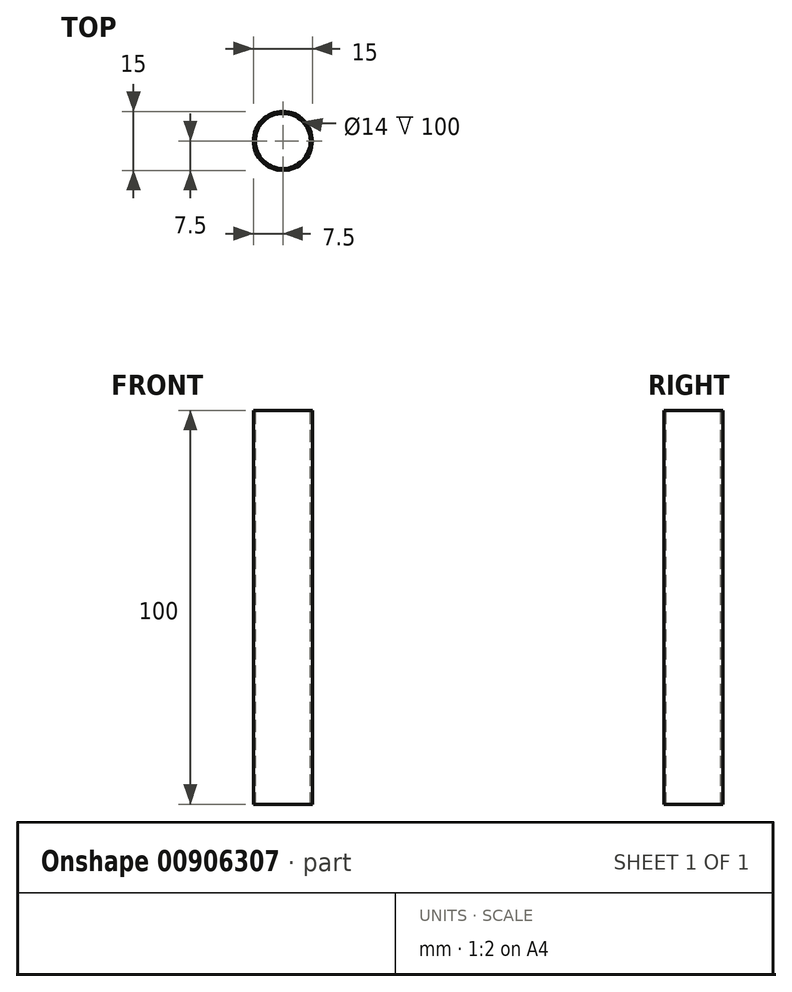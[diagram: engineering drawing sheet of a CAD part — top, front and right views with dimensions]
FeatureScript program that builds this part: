
annotation { "Feature Type Name" : "Feature", "Feature Type Description" : "" }
export const myFeature = defineFeature(function(context is Context, id is Id, definition is map)
    precondition{}
    {
        {
            var Q0;
            Q0=qCreatedBy(makeId("Top.planeOp"),FACE);
            var sketch = newSketch(context, id + "F0", { "sketchPlane" : qUnion([Q0])});
            skCircle(sketch, "E0", {"center": v(0, 0) * mm, "radius": 7.5 * mm});
            skCircle(sketch, "E1", {"center": v(0, 0) * mm, "radius": 7 * mm});
            skSolve(sketch);
        }
        {
            var Q0;
            Q0=qCreatedBy(makeId("Front.planeOp"),FACE);
            var sketch = newSketch(context, id + "F1", { "sketchPlane" : qUnion([Q0])});
            skLineSegment(sketch, "E2", {"start": v(0, 0) * mm, "end": v(0, 100) * mm});
            skSolve(sketch);
        }
        {
            var Q0;
            Q0=makeQuery(id+"F0.imprint","IMPRINT",FACE,{"disambiguationData":[TD([[makeQuery(id+"F0.imprint","IMPRINT",EDGE,{"derivedFrom":sQuery(id+"F0.wireOp",EDGE,"E0")}),1.0]])]});
            var Q1;
            Q1=sQuery(id+"F1.wireOp",EDGE,"E2");
            sweep(context, id + "F2", {"profiles" : qUnion([Q0]), "path" : qUnion([Q1])});
        }
    });
